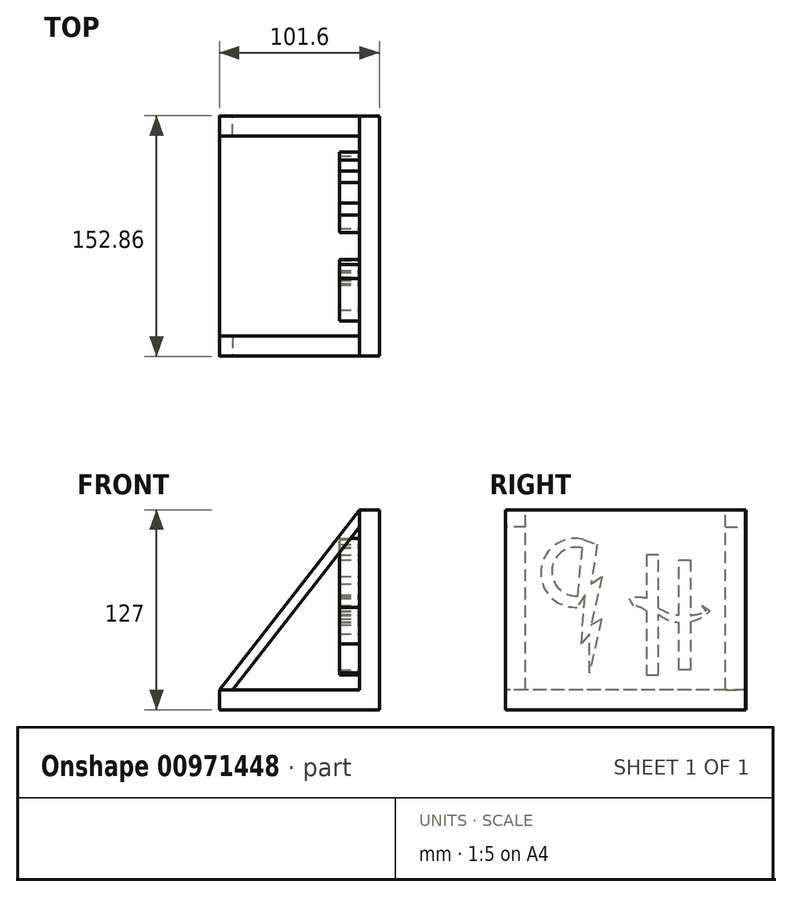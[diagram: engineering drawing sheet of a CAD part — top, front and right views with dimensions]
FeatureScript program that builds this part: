
annotation { "Feature Type Name" : "Feature", "Feature Type Description" : "" }
export const myFeature = defineFeature(function(context is Context, id is Id, definition is map)
    precondition{}
    {
        {
            var Q0;
            Q0=qCreatedBy(makeId("Top.planeOp"),FACE);
            var sketch = newSketch(context, id + "F0", { "sketchPlane" : qUnion([Q0])});
            skLineSegment(sketch, "E0", {"start": v(0, 0) * mm, "end": v(0, 76.2) * mm});
            skLineSegment(sketch, "E1", {"start": v(0, 0) * mm, "end": v(0, -76.2) * mm});
            skLineSegment(sketch, "E2", {"start": v(0, -76.2) * mm, "end": v(-101.6, -76.2) * mm});
            skLineSegment(sketch, "E3", {"start": v(-101.6, -76.2) * mm, "end": v(-101.6, 76.43) * mm});
            skLineSegment(sketch, "E4", {"start": v(-101.6, 76.43) * mm, "end": v(0, 76.2) * mm});
            skSolve(sketch);
        }
        {
            var Q0;
            Q0=makeQuery(id+"F0.imprint","IMPRINT",FACE,{"disambiguationData":[TD([[makeQuery(id+"F0.imprint","IMPRINT",EDGE,{"derivedFrom":sQuery(id+"F0.wireOp",EDGE,"E0")}),1.0]])]});
            extrude(context, id + "F1", {"entities" : qUnion([Q0]), "depth" : 127 * mm, "offsetDistance" : 25.4 * mm});
        }
        {
            var Q0;
            Q0=makeQuery(id+"F1.opExtrude","SWEPT_FACE",FACE,{"disambiguationData":[OSD([sQuery(id+"F0.wireOp",EDGE,"E2")])]});
            var sketch = newSketch(context, id + "F2", { "sketchPlane" : qUnion([Q0])});
            skLineSegment(sketch, "E5", {"start": v(-101.6, 0) * mm, "end": v(-101.6, 12.7) * mm});
            skLineSegment(sketch, "E6", {"start": v(0, 0) * mm, "end": v(-12.7, 0) * mm});
            skLineSegment(sketch, "E7", {"start": v(-12.7, 0) * mm, "end": v(-12.7, 12.7) * mm});
            skLineSegment(sketch, "E8", {"start": v(-12.7, 12.7) * mm, "end": v(-101.6, 12.7) * mm});
            skLineSegment(sketch, "E9", {"start": v(-12.7, 12.7) * mm, "end": v(-12.7, 127) * mm});
            skLineSegment(sketch, "E10", {"start": v(-12.7, 127) * mm, "end": v(-101.6, 127) * mm});
            skLineSegment(sketch, "E11", {"start": v(-101.6, 127) * mm, "end": v(-101.6, 12.7) * mm});
            skSolve(sketch);
        }
        {
            var Q0;
            Q0=makeQuery(id+"F2.imprint","IMPRINT",FACE,{"disambiguationData":[TD([[makeQuery(id+"F2.imprint","IMPRINT",EDGE,{"derivedFrom":sQuery(id+"F2.wireOp",EDGE,"E8")}),-1.0]])]});
            extrude(context, id + "F3", {"entities" : qUnion([Q0]), "operationType" : NewBodyOperationType.REMOVE, "endBound" : BoundingType.THROUGH_ALL, "oppositeDirection" : true, "depth" : 25.4 * mm, "offsetDistance" : 25.4 * mm});
        }
        {
            var Q0;
            Q0=makeQuery(id+"F1.opExtrude","SWEPT_FACE",FACE,{"disambiguationData":[OSD([sQuery(id+"F0.wireOp",EDGE,"E2")])]});
            var sketch = newSketch(context, id + "F4", { "sketchPlane" : qUnion([Q0])});
            skLineSegment(sketch, "E12", {"start": v(-12.7, 127) * mm, "end": v(-9.9, 129.67) * mm});
            skLineSegment(sketch, "E13", {"start": v(-101.6, 12.7) * mm, "end": v(-12.7, 127) * mm});
            skLineSegment(sketch, "E14", {"start": v(-101.6, 12.7) * mm, "end": v(-93.2, 12.7) * mm});
            skLineSegment(sketch, "E15", {"start": v(-93.2, 12.7) * mm, "end": v(-12.7, 116.19) * mm});
            skLineSegment(sketch, "E16", {"start": v(-12.7, 116.19) * mm, "end": v(-12.7, 127) * mm});
            skSolve(sketch);
        }
        {
            var Q0;
            Q0=makeQuery(id+"F4.imprint","IMPRINT",FACE,{"disambiguationData":[TD([[makeQuery(id+"F4.imprint","IMPRINT",EDGE,{"derivedFrom":sQuery(id+"F4.wireOp",EDGE,"E13")}),-1.0]])]});
            extrude(context, id + "F5", {"entities" : qUnion([Q0]), "operationType" : NewBodyOperationType.ADD, "oppositeDirection" : true, "depth" : 12.7 * mm, "offsetDistance" : 25.4 * mm});
        }
        {
            var Q0;
            Q0=makeQuery(id+"F1.opExtrude","SWEPT_BODY",BODY,{"disambiguationData":[OSD([sQuery(id+"F0.wireOp",EDGE,"E0"),sQuery(id+"F0.wireOp",EDGE,"E1"),sQuery(id+"F0.wireOp",EDGE,"E2"),sQuery(id+"F0.wireOp",EDGE,"E3"),sQuery(id+"F0.wireOp",EDGE,"E4")])]});
            var Q1;
            Q1=qCreatedBy(makeId("Front.planeOp"),FACE);
            mirror(context, id + "F6", {"operationType" : NewBodyOperationType.ADD, "entities" : qUnion([Q0]), "mirrorPlane" : qUnion([Q1])});
        }
        {
            var Q0;
            {var subQ0=makeQuery(id+"F3.boolean.opBoolean","COPY",FACE,{"derivedFrom":makeQuery(id+"F3.opExtrude","SWEPT_FACE",FACE,{"disambiguationData":[OSD([sQuery(id+"F2.wireOp",EDGE,"E9")])]})});Q0=makeQuery(id+"F6.boolean.opBoolean","MERGE",FACE,{"derivedFrom":[subQ0,makeQuery(id+"F6.opPattern","COPY",FACE,{"derivedFrom":subQ0,"instanceName":"1"})]});}
            var sketch = newSketch(context, id + "F7", { "sketchPlane" : qUnion([Q0])});
            skLineSegment(sketch, "E17", {"start": v(-41.12, 95.3) * mm, "end": v(-41.12, 25.46) * mm});
            skLineSegment(sketch, "E18", {"start": v(-41.12, 25.46) * mm, "end": v(-33.95, 25.46) * mm});
            skLineSegment(sketch, "E19", {"start": v(-33.95, 25.46) * mm, "end": v(-33.95, 95.3) * mm});
            skLineSegment(sketch, "E20", {"start": v(-33.95, 95.3) * mm, "end": v(-41.12, 95.3) * mm});
            skLineSegment(sketch, "E21", {"start": v(-33.95, 25.46) * mm, "end": v(-33.95, 60.66) * mm});
            skLineSegment(sketch, "E22", {"start": v(-20.8, 60.66) * mm, "end": v(-20.8, 98.4) * mm});
            skLineSegment(sketch, "E23", {"start": v(-20.8, 98.4) * mm, "end": v(-13.18, 98.4) * mm});
            skLineSegment(sketch, "E24", {"start": v(-13.18, 98.4) * mm, "end": v(-13.18, 22.2) * mm});
            skLineSegment(sketch, "E25", {"start": v(-13.18, 22.2) * mm, "end": v(-20.8, 22.2) * mm});
            skLineSegment(sketch, "E26", {"start": v(-20.8, 22.2) * mm, "end": v(-20.8, 60.66) * mm});
            skLineSegment(sketch, "E27", {"start": v(-48.38, 66.3) * mm, "end": v(-53.5, 62.9) * mm});
            skLineSegment(sketch, "E28", {"start": v(-48.38, 66.3) * mm, "end": v(-50.94, 62.43) * mm});
            skPoint(sketch, "E28.endSnap0", {"position": v(-50.94, 64.6) * mm});
            skArc(sketch, "E29", {"start": v(-53.5, 62.9) * mm, "mid": v(-37.58, 55.44) * mm, "end": v(-20.8, 60.66) * mm});
            skArc(sketch, "E30", {"start": v(-50.94, 62.43) * mm, "mid": v(-35.61, 59.96) * mm, "end": v(-20.8, 64.6) * mm});
            skLineSegment(sketch, "E31", {"start": v(-2.16, 70.8) * mm, "end": v(-4.64, 66.3) * mm});
            skArc(sketch, "E32", {"start": v(-4.64, 66.3) * mm, "mid": v(-9.1, 65.09) * mm, "end": v(-13.18, 62.9) * mm});
            skArc(sketch, "E33", {"start": v(-2.16, 70.8) * mm, "mid": v(-7.67, 71.47) * mm, "end": v(-13.18, 70.8) * mm});
            skSolve(sketch);
        }
        {
            var Q0;
            {var subQ0=makeQuery(id+"F3.boolean.opBoolean","COPY",FACE,{"derivedFrom":makeQuery(id+"F3.opExtrude","SWEPT_FACE",FACE,{"disambiguationData":[OSD([sQuery(id+"F2.wireOp",EDGE,"E9")])]})});Q0=makeQuery(id+"F6.boolean.opBoolean","MERGE",FACE,{"derivedFrom":[subQ0,makeQuery(id+"F6.opPattern","COPY",FACE,{"derivedFrom":subQ0,"instanceName":"1"})]});}
            var sketch = newSketch(context, id + "F8", { "sketchPlane" : qUnion([Q0])});
            skLineSegment(sketch, "E34", {"start": v(18.26, 105.03) * mm, "end": v(21.94, 79.9) * mm});
            skLineSegment(sketch, "E35", {"start": v(21.94, 79.9) * mm, "end": v(14.97, 84.86) * mm});
            skLineSegment(sketch, "E36", {"start": v(14.97, 84.86) * mm, "end": v(21.94, 53.93) * mm});
            skLineSegment(sketch, "E37", {"start": v(21.94, 53.93) * mm, "end": v(15.4, 57.66) * mm});
            skLineSegment(sketch, "E38", {"start": v(15.4, 57.66) * mm, "end": v(23.12, 23.45) * mm});
            skLineSegment(sketch, "E39", {"start": v(23.12, 23.45) * mm, "end": v(23.12, 48.23) * mm});
            skLineSegment(sketch, "E40", {"start": v(23.12, 48.23) * mm, "end": v(28.13, 41.87) * mm});
            skLineSegment(sketch, "E41", {"start": v(28.13, 41.87) * mm, "end": v(25.93, 73.01) * mm});
            skLineSegment(sketch, "E42", {"start": v(25.93, 73.01) * mm, "end": v(30.98, 65.12) * mm});
            skLineSegment(sketch, "E43", {"start": v(30.98, 65.12) * mm, "end": v(27.03, 108.32) * mm});
            skLineSegment(sketch, "E44", {"start": v(27.03, 108.32) * mm, "end": v(18.26, 105.03) * mm});
            skArc(sketch, "E45", {"start": v(30.98, 65.12) * mm, "mid": v(53.8, 88.99) * mm, "end": v(27.03, 108.32) * mm});
            skArc(sketch, "E46", {"start": v(30.3, 72.45) * mm, "mid": v(46.8, 89.24) * mm, "end": v(27.54, 102.77) * mm});
            skSolve(sketch);
        }
        {
            var Q0;
            Q0=makeQuery(id+"F8.imprint","IMPRINT",FACE,{"disambiguationData":[TD([[makeQuery(id+"F8.imprint","IMPRINT",EDGE,{"derivedFrom":sQuery(id+"F8.wireOp",EDGE,"E34")}),1.0]])]});
            var Q1;
            {var subQ0=sQuery(id+"F8.wireOp",EDGE,"E45");Q1=makeQuery(id+"F8.imprint","IMPRINT",FACE,{"disambiguationData":[TD([[makeQuery(id+"F8.imprint","IMPRINT",EDGE,{"derivedFrom":subQ0}),1.0]])]});}
            extrude(context, id + "F9", {"entities" : qUnion([Q0, Q1]), "operationType" : NewBodyOperationType.ADD, "depth" : 12.7 * mm, "offsetDistance" : 25.4 * mm});
        }
        {
            var Q0;
            {var subQ3=sQuery(id+"F7.wireOp",EDGE,"E27");Q0=makeQuery(id+"F7.imprint","IMPRINT",FACE,{"disambiguationData":[TD([[makeQuery(id+"F7.imprint","IMPRINT",EDGE,{"derivedFrom":subQ3}),1.0]])]});}
            var Q1;
            {var subQ0=sQuery(id+"F7.wireOp",EDGE,"E20");Q1=makeQuery(id+"F7.imprint","IMPRINT",FACE,{"disambiguationData":[TD([[makeQuery(id+"F7.imprint","IMPRINT",EDGE,{"derivedFrom":subQ0}),1.0]])]});}
            var Q2;
            {var subQ3=sQuery(id+"F7.wireOp",EDGE,"E18");Q2=makeQuery(id+"F7.imprint","IMPRINT",FACE,{"disambiguationData":[TD([[makeQuery(id+"F7.imprint","IMPRINT",EDGE,{"derivedFrom":subQ3}),1.0]])]});}
            var Q3;
            {var subQ0=sQuery(id+"F7.wireOp",EDGE,"E29");var subQ1=sQuery(id+"F7.wireOp",EDGE,"E17");var subQ2=makeQuery(id+"F7.imprint","INTERSECT",VERTEX,{"derivedFrom":[subQ1,subQ0]});Q3=makeQuery(id+"F7.imprint","IMPRINT",FACE,{"disambiguationData":[TD([[makeQuery(id+"F7.imprint","IMPRINT",EDGE,{"disambiguationData":[TD([[subQ2,1.0]])],"derivedFrom":subQ1}),1.0]])]});}
            var Q4;
            {var subQ0=sQuery(id+"F7.wireOp",EDGE,"E29");var subQ1=sQuery(id+"F7.wireOp",EDGE,"E19");var subQ2=makeQuery(id+"F7.imprint","INTERSECT",VERTEX,{"derivedFrom":[subQ1,subQ0]});Q4=makeQuery(id+"F7.imprint","IMPRINT",FACE,{"disambiguationData":[TD([[makeQuery(id+"F7.imprint","IMPRINT",EDGE,{"disambiguationData":[TD([[subQ2,-1.0]])],"derivedFrom":subQ1}),-1.0]])]});}
            var Q5;
            {var subQ3=sQuery(id+"F7.wireOp",EDGE,"E23");Q5=makeQuery(id+"F7.imprint","IMPRINT",FACE,{"disambiguationData":[TD([[makeQuery(id+"F7.imprint","IMPRINT",EDGE,{"derivedFrom":subQ3}),-1.0]])]});}
            var Q6;
            Q6=makeQuery(id+"F7.imprint","IMPRINT",FACE,{"disambiguationData":[TD([[makeQuery(id+"F7.imprint","IMPRINT",EDGE,{"derivedFrom":sQuery(id+"F7.wireOp",EDGE,"E31")}),-1.0]])]});
            extrude(context, id + "F10", {"entities" : qUnion([Q0, Q1, Q2, Q3, Q4, Q5, Q6]), "operationType" : NewBodyOperationType.ADD, "depth" : 12.7 * mm, "offsetDistance" : 25.4 * mm});
        }
    });
